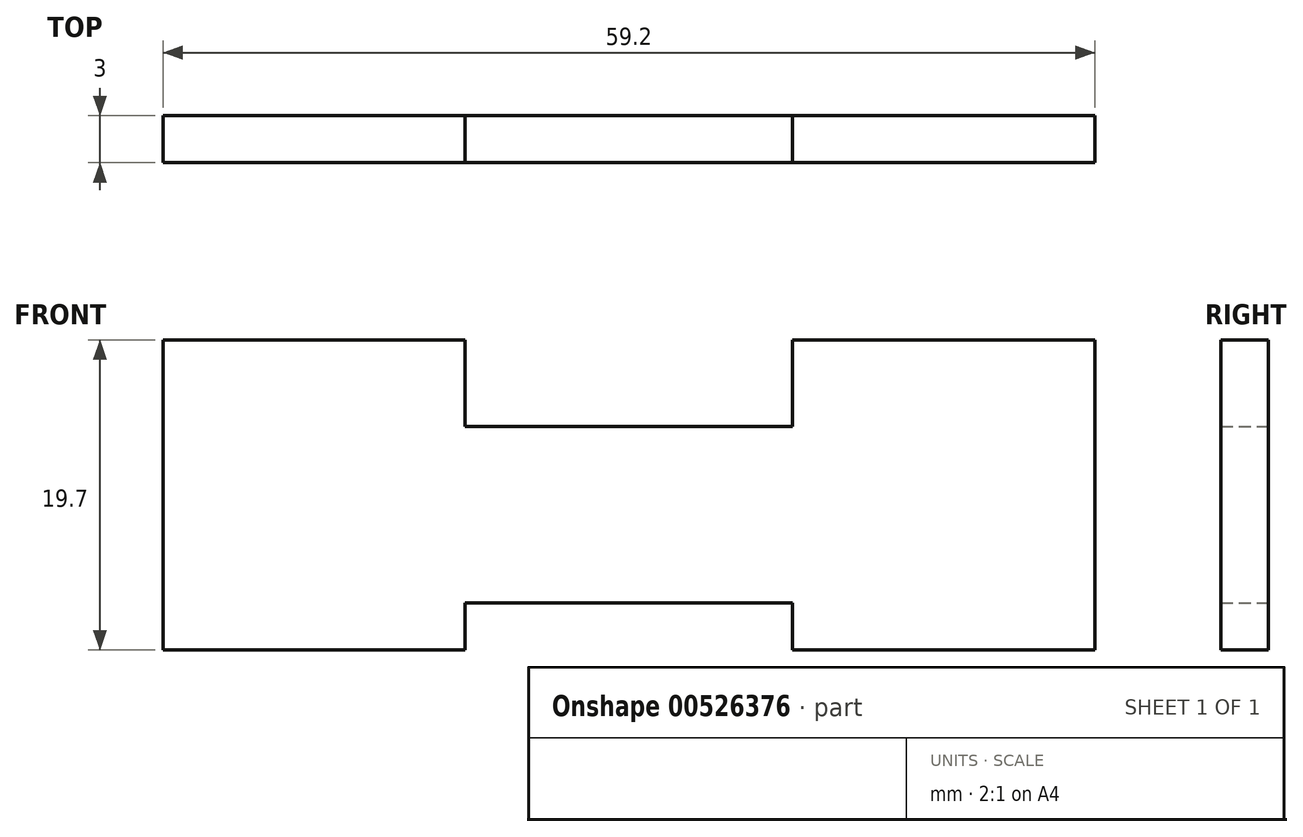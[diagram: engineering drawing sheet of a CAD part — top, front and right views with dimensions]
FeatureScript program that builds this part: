
annotation { "Feature Type Name" : "Feature", "Feature Type Description" : "" }
export const myFeature = defineFeature(function(context is Context, id is Id, definition is map)
    precondition{}
    {
        {
            assignVariable(context, id + "F0", {"name" : "thickness", "anyValue" : 3});
        }
        {
            var Q0;
            Q0=qCreatedBy(makeId("Front.planeOp"),FACE);
            var sketch = newSketch(context, id + "F1", { "sketchPlane" : qUnion([Q0])});
            skLineSegment(sketch, "E0.top", {"start": v(30, 10.25) * mm, "end": v(-30, 10.25) * mm, "construction": true});
            skLineSegment(sketch, "E0.left", {"start": v(30, -10.25) * mm, "end": v(30, 10.25) * mm, "construction": true});
            skLineSegment(sketch, "E0.right", {"start": v(-30, -10.25) * mm, "end": v(-30, 10.25) * mm, "construction": true});
            skPoint(sketch, "E0.middle", {"position": v(0, 0) * mm});
            skLineSegment(sketch, "E1", {"start": v(-30, -10.25) * mm, "end": v(-10, -10.25) * mm, "construction": true});
            skLineSegment(sketch, "E2", {"start": v(-10, -10.25) * mm, "end": v(-10, -7.25) * mm});
            skLineSegment(sketch, "E3", {"start": v(-10, -7.25) * mm, "end": v(10, -7.25) * mm, "construction": true});
            skLineSegment(sketch, "E4", {"start": v(10, -7.25) * mm, "end": v(10, -10.25) * mm});
            skLineSegment(sketch, "E5", {"start": v(10, -10.25) * mm, "end": v(30, -10.25) * mm, "construction": true});
            skLineSegment(sketch, "E6", {"start": v(-30, 10.25) * mm, "end": v(-10, 10.25) * mm});
            skLineSegment(sketch, "E7", {"start": v(-10, 10.25) * mm, "end": v(-10, 4.75) * mm, "construction": true});
            skLineSegment(sketch, "E8", {"start": v(-10, 4.75) * mm, "end": v(10, 4.75) * mm, "construction": true});
            skLineSegment(sketch, "E9", {"start": v(10, 4.75) * mm, "end": v(10, 10.25) * mm, "construction": true});
            skLineSegment(sketch, "E10", {"start": v(10, 10.25) * mm, "end": v(30, 10.25) * mm});
            skLineSegment(sketch, "E11.0", {"start": v(10.4, -6.85) * mm, "end": v(10.4, -9.85) * mm});
            skLineSegment(sketch, "E11.1", {"start": v(-10.4, 4.35) * mm, "end": v(10.4, 4.35) * mm});
            skLineSegment(sketch, "E11.2", {"start": v(10.4, 4.35) * mm, "end": v(10.4, 9.85) * mm});
            skLineSegment(sketch, "E11.3", {"start": v(10.4, 9.85) * mm, "end": v(29.6, 9.85) * mm});
            skLineSegment(sketch, "E11.4", {"start": v(29.6, -9.85) * mm, "end": v(29.6, 9.85) * mm});
            skLineSegment(sketch, "E11.5", {"start": v(-10.4, 9.85) * mm, "end": v(-10.4, 4.35) * mm});
            skLineSegment(sketch, "E11.6", {"start": v(10.4, -9.85) * mm, "end": v(29.6, -9.85) * mm});
            skLineSegment(sketch, "E11.7", {"start": v(-29.6, 9.85) * mm, "end": v(-10.4, 9.85) * mm});
            skLineSegment(sketch, "E11.8", {"start": v(-29.6, -9.85) * mm, "end": v(-29.6, 9.85) * mm});
            skLineSegment(sketch, "E11.9", {"start": v(-29.6, -9.85) * mm, "end": v(-10.4, -9.85) * mm});
            skLineSegment(sketch, "E11.10", {"start": v(-10.4, -9.85) * mm, "end": v(-10.4, -6.85) * mm});
            skLineSegment(sketch, "E11.11", {"start": v(-10.4, -6.85) * mm, "end": v(10.4, -6.85) * mm});
            skSolve(sketch);
        }
        {
            var Q0;
            Q0 = qSketchRegion(id + "F1", true);
            extrude(context, id + "F2", {"entities" : qUnion([Q0]), "depth" : (getVariable(context, 'thickness')) * mm, "offsetDistance" : 25 * mm});
        }
    });
